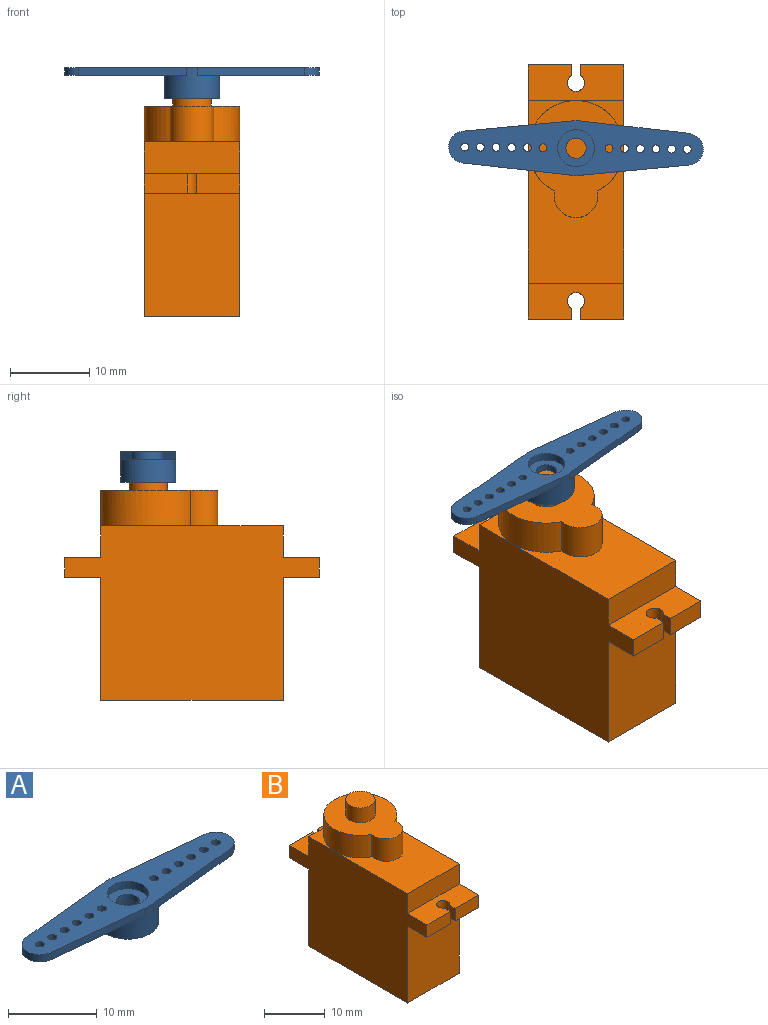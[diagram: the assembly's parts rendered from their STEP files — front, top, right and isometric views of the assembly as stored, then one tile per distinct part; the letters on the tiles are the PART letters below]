
ASSEMBLY  parts=2 mates=1
PART A: 28 faces, bbox 32x7x3.9 mm
  f0: cylinder r=3.47mm len=6.95mm, axis (0,0,-1), area 65.1mm2, adj f1,f2,f5,f6,f8,f18,f19,f21
  f1: plane 32.05x6.95mm, normal (0,0,1), area 140.4mm2, adj f0,f5,f6,f7,f9,f12,f13,f14
  f2: plane 6.95x6.95mm, normal (0,0,-1), area 19.5mm2, adj f0,f3
  f3: cylinder r=2.43mm len=4.85mm, axis (0,0,-1), area 30.5mm2, adj f2,f4
  f4: plane 4.85x4.85mm, normal (0,0,-1), area 13.4mm2, adj f3,f11
  f5: plane 13.51x1.4mm, normal (0.1,0.99,0), area 13.6mm2, adj f0,f1,f7,f8
  f6: plane 13.51x1.4mm, normal (0.1,-0.99,0), area 13.6mm2, adj f0,f1,f7,f8
  f7: cylinder r=2.01mm len=4mm, axis (0,0,1), area 5.9mm2, adj f1,f5,f6,f8
  f8: plane 15.31x6.8mm, normal (0,0,-1), area 59.7mm2, adj f0,f5,f6,f7,f12,f13,f14,f15
  f9: cylinder r=2.32mm len=4.65mm, axis (0,0,1), area 14.6mm2, adj f1,f10
  f10: plane 4.65x4.65mm, normal (0,0,1), area 11.9mm2, adj f9,f11
  f11: cylinder r=1.28mm len=2.55mm, axis (0,0,1), area 6.8mm2, adj f4,f10
  f12: cylinder r=0.5mm len=1mm, axis (0,0,1), area 3.1mm2, adj f1,f8
  f13: cylinder r=0.5mm len=1mm, axis (0,0,1), area 3.1mm2, adj f1,f8
  f14: cylinder r=0.5mm len=1mm, axis (0,0,1), area 3.1mm2, adj f1,f8
  f15: cylinder r=0.5mm len=1mm, axis (0,0,1), area 3.1mm2, adj f1,f8
  f16: cylinder r=0.5mm len=1mm, axis (0,0,1), area 3.1mm2, adj f1,f8
  f17: cylinder r=0.5mm len=1mm, axis (0,0,1), area 3.1mm2, adj f1,f8
  f18: plane 13.51x1.4mm, normal (-0.1,0.99,0), area 13.6mm2, adj f0,f1,f20,f21
  f19: plane 13.51x1.4mm, normal (-0.1,-0.99,0), area 13.6mm2, adj f0,f1,f20,f21
  f20: cylinder r=2.01mm len=4mm, axis (0,0,1), area 5.9mm2, adj f1,f18,f19,f21
  f21: plane 15.31x6.8mm, normal (0,0,-1), area 59.7mm2, adj f0,f18,f19,f20,f22,f23,f24,f25
  f22: cylinder r=0.5mm len=1mm, axis (0,0,1), area 3.1mm2, adj f1,f21
  f23: cylinder r=0.5mm len=1mm, axis (0,0,1), area 3.1mm2, adj f1,f21
  f24: cylinder r=0.5mm len=1mm, axis (0,0,1), area 3.1mm2, adj f1,f21
  f25: cylinder r=0.5mm len=1mm, axis (0,0,1), area 3.1mm2, adj f1,f21
  f26: cylinder r=0.5mm len=1mm, axis (0,0,1), area 3.1mm2, adj f1,f21
  f27: cylinder r=0.5mm len=1mm, axis (0,0,1), area 3.1mm2, adj f1,f21
PART B: 29 faces, bbox 12x32x29.5 mm
  f0: plane 17x12mm, normal (0,0,1), area 134.4mm2, adj f9,f10,f11,f24,f25
  f1: plane 6x6mm, normal (0,0,1), area 7.7mm2, adj f8,f11,f25
  f2: plane 5.43x2.5mm, normal (0,1,0), area 13.6mm2, adj f4,f5,f11,f22
  f3: plane 5.43x2.5mm, normal (0,-1,0), area 13.6mm2, adj f11,f16,f17,f19
  f4: plane 12x4.5mm, normal (0,0,1), area 49mm2, adj f2,f8,f9,f11,f14,f21,f22,f23
  f5: plane 12x4.5mm, normal (0,0,-1), area 49mm2, adj f2,f7,f9,f11,f14,f21,f22,f23
  f6: plane 15.5x12mm, normal (0,-1,0), area 186mm2, adj f9,f11,f13,f17
  f7: plane 15.5x12mm, normal (0,1,0), area 186mm2, adj f5,f9,f11,f13
  f8: plane 12x4mm, normal (0,1,0), area 48mm2, adj f1,f4,f9,f11,f12
  f9: plane 32x22mm, normal (-1,0,0), area 528.5mm2, adj f0,f4,f5,f6,f7,f8,f10,f12
  f10: plane 12x4mm, normal (0,-1,0), area 48mm2, adj f0,f9,f11,f16
  f11: plane 32x22mm, normal (1,0,0), area 528.5mm2, adj f0,f1,f2,f3,f4,f5,f6,f7
  f12: plane 6x6mm, normal (0,0,1), area 7.7mm2, adj f8,f9,f25
  f13: plane 23x12mm, normal (0,0,-1), area 276mm2, adj f6,f7,f9,f11
  f14: plane 5.43x2.5mm, normal (0,1,0), area 13.6mm2, adj f4,f5,f9,f23
  f15: plane 5.43x2.5mm, normal (0,-1,0), area 13.6mm2, adj f9,f16,f17,f18
  f16: plane 12x4.5mm, normal (0,0,1), area 49mm2, adj f3,f9,f10,f11,f15,f18,f19,f20
  f17: plane 12x4.5mm, normal (0,0,-1), area 49mm2, adj f3,f6,f9,f11,f15,f18,f19,f20
  f18: plane 2.5x1.34mm, normal (1,0,0), area 3.4mm2, adj f15,f16,f17,f20
  f19: plane 2.5x1.34mm, normal (-1,0,0), area 3.4mm2, adj f3,f16,f17,f20
  f20: cylinder r=1.07mm len=2.5mm, axis (0,0,1), area 13.9mm2, adj f16,f17,f18,f19
  f21: cylinder r=1.07mm len=2.5mm, axis (0,0,1), area 13.9mm2, adj f4,f5,f22,f23
  f22: plane 2.5x1.34mm, normal (-1,0,0), area 3.4mm2, adj f2,f4,f5,f21
  f23: plane 2.5x1.34mm, normal (1,0,0), area 3.4mm2, adj f4,f5,f14,f21
  f24: cylinder r=2.75mm len=5.5mm, axis (0,0,-1), area 44.6mm2, adj f0,f25,f26
  f25: cylinder r=6mm len=12mm, axis (0,0,-1), area 144.7mm2, adj f0,f1,f12,f24,f26
  f26: plane 14.75x12mm, normal (0,0,1), area 107.7mm2, adj f24,f25,f27
  f27: cylinder r=2.43mm len=4.85mm, axis (0,0,-1), area 45.7mm2, adj f26,f28
  f28: plane 4.85x4.85mm, normal (0,0,1), area 18.5mm2, adj f27
PLACE A rot(axis=(0,0,-1),0.6deg) t=(0,5.5,27.5)mm
PLACE B t=(-6,-11.5,0)mm
MATE revolute A.f0 <-> B.f25  axis (0,0,-1) through (0,5.5,29.5)mm
